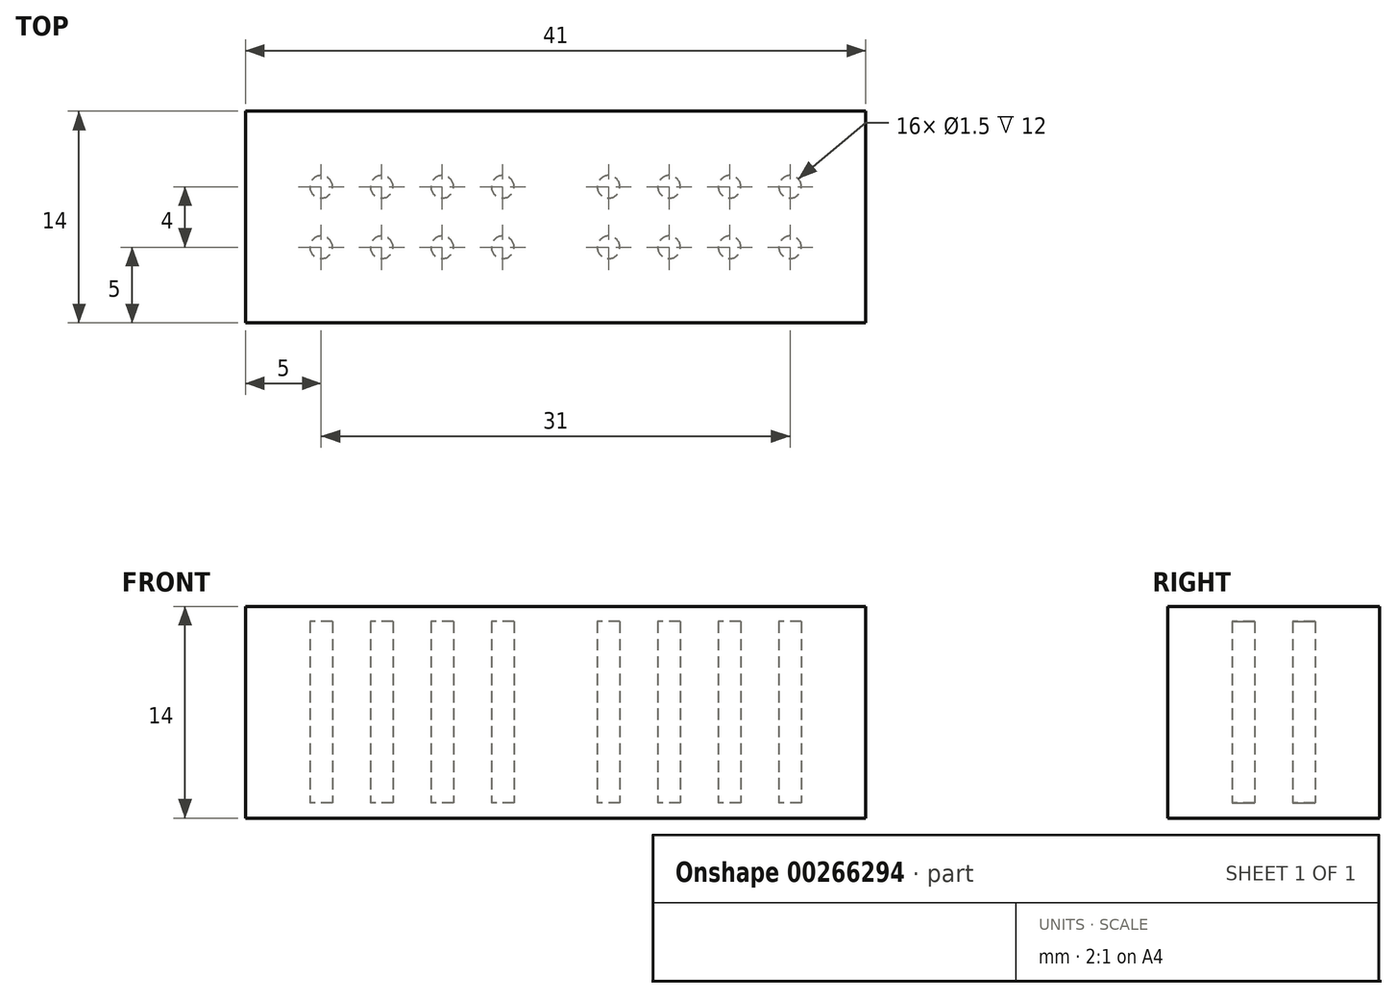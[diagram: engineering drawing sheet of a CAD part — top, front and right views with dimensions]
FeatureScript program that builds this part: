
annotation { "Feature Type Name" : "Feature", "Feature Type Description" : "" }
export const myFeature = defineFeature(function(context is Context, id is Id, definition is map)
    precondition{}
    {
        {
            var Q0;
            Q0=qCreatedBy(makeId("Top.planeOp"),FACE);
            var sketch = newSketch(context, id + "F0", { "sketchPlane" : qUnion([Q0])});
            skLineSegment(sketch, "E0.bottom", {"start": v(20.5, -7) * mm, "end": v(-20.5, -7) * mm});
            skLineSegment(sketch, "E0.top", {"start": v(20.5, 7) * mm, "end": v(-20.5, 7) * mm});
            skLineSegment(sketch, "E0.left", {"start": v(20.5, -7) * mm, "end": v(20.5, 7) * mm});
            skLineSegment(sketch, "E0.right", {"start": v(-20.5, -7) * mm, "end": v(-20.5, 7) * mm});
            skPoint(sketch, "E0.middle", {"position": v(0, 0) * mm});
            skSolve(sketch);
        }
        {
            var Q0;
            Q0 = qSketchRegion(id + "F0", true);
            extrude(context, id + "F1", {"entities" : qUnion([Q0]), "depth" : 1 * mm});
        }
        {
            var Q0;
            Q0=makeQuery(id+"F1.opExtrude","CAP_FACE",FACE,{"disambiguationData":[OSD([sQuery(id+"F0.wireOp",EDGE,"E0.bottom"),sQuery(id+"F0.wireOp",EDGE,"E0.top"),sQuery(id+"F0.wireOp",EDGE,"E0.left"),sQuery(id+"F0.wireOp",EDGE,"E0.right")])],"isStart":false});
            var sketch = newSketch(context, id + "F2", { "sketchPlane" : qUnion([Q0])});
            skLineSegment(sketch, "E1.bottom", {"start": v(-19.5, -6) * mm, "end": v(19.5, -6) * mm});
            skLineSegment(sketch, "E1.top", {"start": v(-19.5, 6) * mm, "end": v(19.5, 6) * mm});
            skLineSegment(sketch, "E1.left", {"start": v(-19.5, -6) * mm, "end": v(-19.5, 6) * mm});
            skLineSegment(sketch, "E1.right", {"start": v(19.5, -6) * mm, "end": v(19.5, 6) * mm});
            skPoint(sketch, "E1.middle", {"position": v(0, 0) * mm});
            skCircle(sketch, "E2", {"center": v(-15.5, 2) * mm, "radius": 0.75 * mm});
            skCircle(sketch, "E3", {"center": v(-15.5, -2) * mm, "radius": 0.75 * mm});
            skCircle(sketch, "E4", {"center": v(-11.5, 2) * mm, "radius": 0.75 * mm});
            skCircle(sketch, "E5", {"center": v(-11.5, -2) * mm, "radius": 0.75 * mm});
            skCircle(sketch, "E6", {"center": v(-7.5, 2) * mm, "radius": 0.75 * mm});
            skCircle(sketch, "E7", {"center": v(-7.5, -2) * mm, "radius": 0.75 * mm});
            skCircle(sketch, "E8", {"center": v(-3.5, 2) * mm, "radius": 0.75 * mm});
            skCircle(sketch, "E9", {"center": v(-3.5, -2) * mm, "radius": 0.75 * mm});
            skCircle(sketch, "E10", {"center": v(3.5, 2) * mm, "radius": 0.75 * mm});
            skCircle(sketch, "E11", {"center": v(3.5, -2) * mm, "radius": 0.75 * mm});
            skCircle(sketch, "E12", {"center": v(7.5, 2) * mm, "radius": 0.75 * mm});
            skCircle(sketch, "E13", {"center": v(7.5, -2) * mm, "radius": 0.75 * mm});
            skCircle(sketch, "E14", {"center": v(11.5, 2) * mm, "radius": 0.75 * mm});
            skCircle(sketch, "E15", {"center": v(11.5, -2) * mm, "radius": 0.75 * mm});
            skCircle(sketch, "E16", {"center": v(15.5, 2) * mm, "radius": 0.75 * mm});
            skCircle(sketch, "E17", {"center": v(15.5, -2) * mm, "radius": 0.75 * mm});
            skSolve(sketch);
        }
        {
            var Q0;
            Q0=makeQuery(id+"F2.imprint","IMPRINT",FACE,{"disambiguationData":[TD([[makeQuery(id+"F2.imprint","IMPRINT",EDGE,{"derivedFrom":sQuery(id+"F2.wireOp",EDGE,"E1.bottom")}),-1.0]])]});
            extrude(context, id + "F3", {"entities" : qUnion([Q0]), "operationType" : NewBodyOperationType.ADD, "depth" : 12 * mm});
        }
        {
            var Q0;
            Q0 = qSketchRegion(id + "F2", true);
            extrude(context, id + "F4", {"entities" : qUnion([Q0]), "operationType" : NewBodyOperationType.ADD, "depth" : 12 * mm});
        }
        {
            var Q0;
            {var subQ0=sQuery(id+"F2.wireOp",EDGE,"E1.right");var subQ1=sQuery(id+"F2.wireOp",EDGE,"E1.left");var subQ2=sQuery(id+"F2.wireOp",EDGE,"E1.top");var subQ3=sQuery(id+"F2.wireOp",EDGE,"E1.bottom");Q0=makeQuery(id+"F4.boolean.opBoolean","MERGE",FACE,{"derivedFrom":[makeQuery(id+"F3.opExtrude","CAP_FACE",FACE,{"disambiguationData":[OSD([sQuery(id+"F0.wireOp",EDGE,"E0.bottom"),sQuery(id+"F0.wireOp",EDGE,"E0.top"),sQuery(id+"F0.wireOp",EDGE,"E0.left"),sQuery(id+"F0.wireOp",EDGE,"E0.right"),subQ3,subQ2,subQ1,subQ0])],"isStart":false}),makeQuery(id+"F4.opExtrude","CAP_FACE",FACE,{"disambiguationData":[OSD([subQ3,subQ2,subQ1,subQ0,sQuery(id+"F2.wireOp",EDGE,"E2"),sQuery(id+"F2.wireOp",EDGE,"E3"),sQuery(id+"F2.wireOp",EDGE,"E4"),sQuery(id+"F2.wireOp",EDGE,"E5"),sQuery(id+"F2.wireOp",EDGE,"E6"),sQuery(id+"F2.wireOp",EDGE,"E7"),sQuery(id+"F2.wireOp",EDGE,"E8"),sQuery(id+"F2.wireOp",EDGE,"E9"),sQuery(id+"F2.wireOp",EDGE,"E10"),sQuery(id+"F2.wireOp",EDGE,"E11"),sQuery(id+"F2.wireOp",EDGE,"E12"),sQuery(id+"F2.wireOp",EDGE,"E13"),sQuery(id+"F2.wireOp",EDGE,"E14"),sQuery(id+"F2.wireOp",EDGE,"E15"),sQuery(id+"F2.wireOp",EDGE,"E16"),sQuery(id+"F2.wireOp",EDGE,"E17")])],"isStart":false})]});}
            var sketch = newSketch(context, id + "F5", { "sketchPlane" : qUnion([Q0])});
            skLineSegment(sketch, "E18.0.0", {"start": v(-20.5, -7) * mm, "end": v(20.5, -7) * mm});
            skLineSegment(sketch, "E18.0.1", {"start": v(20.5, -7) * mm, "end": v(20.5, 7) * mm});
            skLineSegment(sketch, "E18.0.2", {"start": v(20.5, 7) * mm, "end": v(-20.5, 7) * mm});
            skLineSegment(sketch, "E18.0.3", {"start": v(-20.5, 7) * mm, "end": v(-20.5, -7) * mm});
            skSolve(sketch);
        }
        {
            var Q0;
            Q0 = qSketchRegion(id + "F5", true);
            extrude(context, id + "F6", {"entities" : qUnion([Q0]), "operationType" : NewBodyOperationType.ADD, "depth" : 1 * mm});
        }
    });
